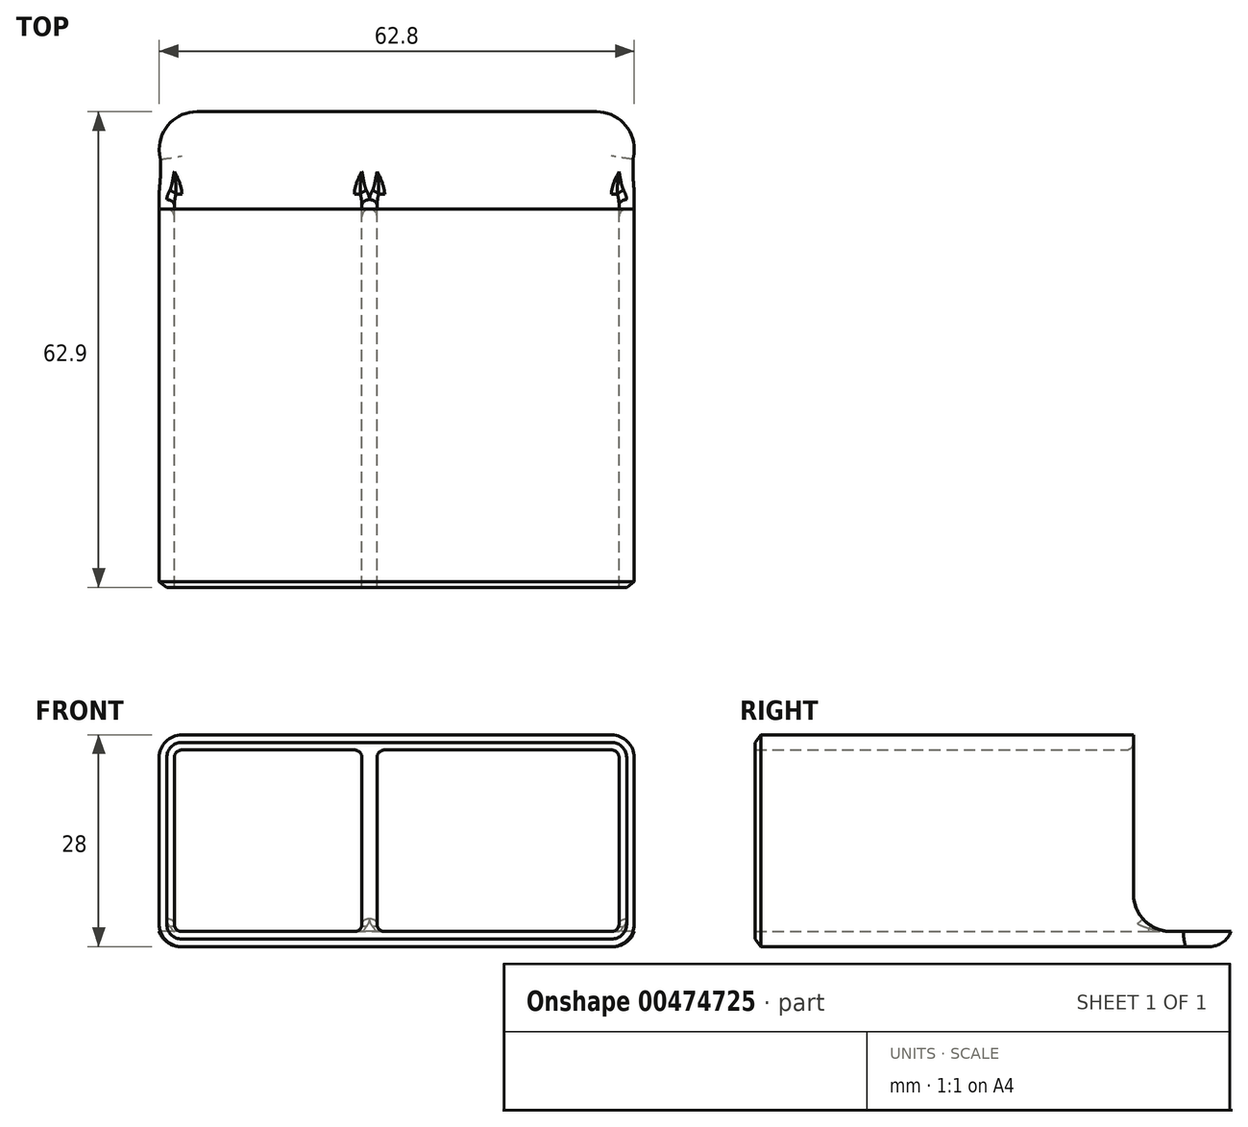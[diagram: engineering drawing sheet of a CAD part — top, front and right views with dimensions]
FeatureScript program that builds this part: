
annotation { "Feature Type Name" : "Feature", "Feature Type Description" : "" }
export const myFeature = defineFeature(function(context is Context, id is Id, definition is map)
    precondition{}
    {
        {
            var Q0;
            Q0=qCreatedBy(makeId("Front.planeOp"),FACE);
            var sketch = newSketch(context, id + "F0", { "sketchPlane" : qUnion([Q0])});
            skLineSegment(sketch, "E0.bottom", {"start": v(0, 0) * mm, "end": v(62.8, 0) * mm});
            skLineSegment(sketch, "E0.top", {"start": v(0, 28) * mm, "end": v(62.8, 28) * mm});
            skLineSegment(sketch, "E0.left", {"start": v(0, 0) * mm, "end": v(0, 28) * mm});
            skLineSegment(sketch, "E0.right", {"start": v(62.8, 0) * mm, "end": v(62.8, 28) * mm});
            skLineSegment(sketch, "E1.bottom", {"start": v(28.8, 26) * mm, "end": v(60.8, 26) * mm});
            skLineSegment(sketch, "E1.top", {"start": v(28.8, 2) * mm, "end": v(60.8, 2) * mm});
            skLineSegment(sketch, "E1.left", {"start": v(28.8, 26) * mm, "end": v(28.8, 2) * mm});
            skLineSegment(sketch, "E1.right", {"start": v(60.8, 26) * mm, "end": v(60.8, 2) * mm});
            skLineSegment(sketch, "E2.bottom", {"start": v(2, 26) * mm, "end": v(26.8, 26) * mm});
            skLineSegment(sketch, "E2.top", {"start": v(2, 2) * mm, "end": v(26.8, 2) * mm});
            skLineSegment(sketch, "E2.left", {"start": v(2, 26) * mm, "end": v(2, 2) * mm});
            skLineSegment(sketch, "E2.right", {"start": v(26.8, 26) * mm, "end": v(26.8, 2) * mm});
            skSolve(sketch);
        }
        {
            var Q0;
            Q0 = qSketchRegion(id + "F0", true);
            extrude(context, id + "F1", {"entities" : qUnion([Q0]), "depth" : 62.9 * mm, "offsetDistance" : 25 * mm});
        }
        {
            var Q0;
            Q0=makeQuery(id+"F1.opExtrude","SWEPT_FACE",FACE,{"disambiguationData":[OSD([sQuery(id+"F0.wireOp",EDGE,"E0.top")])]});
            var sketch = newSketch(context, id + "F2", { "sketchPlane" : qUnion([Q0])});
            skLineSegment(sketch, "E3.bottom", {"start": v(0, 0) * mm, "end": v(62.8, 0) * mm});
            skLineSegment(sketch, "E3.top", {"start": v(0, -12.9) * mm, "end": v(62.8, -12.9) * mm});
            skLineSegment(sketch, "E3.left", {"start": v(0, 0) * mm, "end": v(0, -12.9) * mm});
            skLineSegment(sketch, "E3.right", {"start": v(62.8, 0) * mm, "end": v(62.8, -12.9) * mm});
            skSolve(sketch);
        }
        {
            var Q0;
            Q0 = qSketchRegion(id + "F2", true);
            var Q1;
            Q1=makeQuery(id+"F1.opExtrude","SWEPT_FACE",FACE,{"disambiguationData":[OSD([sQuery(id+"F0.wireOp",EDGE,"E1.top")])]});
            extrude(context, id + "F3", {"entities" : qUnion([Q0]), "operationType" : NewBodyOperationType.REMOVE, "endBound" : BoundingType.UP_TO_SURFACE, "oppositeDirection" : true, "depth" : 25 * mm, "endBoundEntityFace" : qUnion([Q1]), "offsetDistance" : 25 * mm});
        }
        {
            var Q0;
            Q0=makeQuery(id+"F1.opExtrude","CAP_EDGE",EDGE,{"disambiguationData":[OSD([sQuery(id+"F0.wireOp",EDGE,"E0.right")])],"isStart":true});
            var Q1;
            Q1=makeQuery(id+"F1.opExtrude","CAP_EDGE",EDGE,{"disambiguationData":[OSD([sQuery(id+"F0.wireOp",EDGE,"E0.left")])],"isStart":true});
            fillet(context, id + "F4", {"entities" : qUnion([Q0, Q1]), "radius" : 5 * mm, "tangentPropagation" : true, "allowEdgeOverflow" : false});
        }
        {
            var Q0;
            {var subQ0=sQuery(id+"F2.wireOp",EDGE,"E3.top");Q0=makeQuery(id+"F3.boolean.opBoolean","COPY",EDGE,{"disambiguationData":[TD([makeQuery(id+"F1.opExtrude","SWEPT_FACE",FACE,{"disambiguationData":[OSD([sQuery(id+"F0.wireOp",EDGE,"E0.right")])]})])],"derivedFrom":makeQuery(id+"F3.opExtrude","CAP_EDGE",EDGE,{"disambiguationData":[OSD([subQ0])],"isStart":false})});}
            var Q1;
            {var subQ0=sQuery(id+"F2.wireOp",EDGE,"E3.top");Q1=makeQuery(id+"F3.boolean.opBoolean","COPY",EDGE,{"disambiguationData":[TD([makeQuery(id+"F1.opExtrude","SWEPT_FACE",FACE,{"disambiguationData":[OSD([sQuery(id+"F0.wireOp",EDGE,"E1.left")])]})])],"derivedFrom":makeQuery(id+"F3.opExtrude","CAP_EDGE",EDGE,{"disambiguationData":[OSD([subQ0])],"isStart":false})});}
            var Q2;
            {var subQ0=sQuery(id+"F2.wireOp",EDGE,"E3.top");Q2=makeQuery(id+"F3.boolean.opBoolean","COPY",EDGE,{"disambiguationData":[TD([makeQuery(id+"F1.opExtrude","SWEPT_FACE",FACE,{"disambiguationData":[OSD([sQuery(id+"F0.wireOp",EDGE,"E0.left")])]})])],"derivedFrom":makeQuery(id+"F3.opExtrude","CAP_EDGE",EDGE,{"disambiguationData":[OSD([subQ0])],"isStart":false})});}
            fillet(context, id + "F5", {"entities" : qUnion([Q0, Q1, Q2]), "radius" : 5 * mm, "tangentPropagation" : true, "allowEdgeOverflow" : false});
        }
        {
            var Q0;
            Q0=makeQuery(id+"F1.opExtrude","SWEPT_EDGE",EDGE,{"disambiguationData":[OSD([sQuery(id+"F0.wireOp",EDGE,"E1.top"),sQuery(id+"F0.wireOp",EDGE,"E1.right")])]});
            var Q1;
            Q1=makeQuery(id+"F1.opExtrude","SWEPT_EDGE",EDGE,{"disambiguationData":[OSD([sQuery(id+"F0.wireOp",EDGE,"E1.bottom"),sQuery(id+"F0.wireOp",EDGE,"E1.right")])]});
            var Q2;
            Q2=makeQuery(id+"F1.opExtrude","SWEPT_EDGE",EDGE,{"disambiguationData":[OSD([sQuery(id+"F0.wireOp",EDGE,"E1.bottom"),sQuery(id+"F0.wireOp",EDGE,"E1.left")])]});
            var Q3;
            Q3=makeQuery(id+"F1.opExtrude","SWEPT_EDGE",EDGE,{"disambiguationData":[OSD([sQuery(id+"F0.wireOp",EDGE,"E1.top"),sQuery(id+"F0.wireOp",EDGE,"E1.left")])]});
            var Q4;
            Q4=makeQuery(id+"F1.opExtrude","SWEPT_EDGE",EDGE,{"disambiguationData":[OSD([sQuery(id+"F0.wireOp",EDGE,"E2.top"),sQuery(id+"F0.wireOp",EDGE,"E2.right")])]});
            var Q5;
            Q5=makeQuery(id+"F1.opExtrude","SWEPT_EDGE",EDGE,{"disambiguationData":[OSD([sQuery(id+"F0.wireOp",EDGE,"E2.bottom"),sQuery(id+"F0.wireOp",EDGE,"E2.right")])]});
            var Q6;
            Q6=makeQuery(id+"F1.opExtrude","SWEPT_EDGE",EDGE,{"disambiguationData":[OSD([sQuery(id+"F0.wireOp",EDGE,"E2.bottom"),sQuery(id+"F0.wireOp",EDGE,"E2.left")])]});
            var Q7;
            Q7=makeQuery(id+"F1.opExtrude","SWEPT_EDGE",EDGE,{"disambiguationData":[OSD([sQuery(id+"F0.wireOp",EDGE,"E2.top"),sQuery(id+"F0.wireOp",EDGE,"E2.left")])]});
            fillet(context, id + "F6", {"entities" : qUnion([Q0, Q1, Q2, Q3, Q4, Q5, Q6, Q7]), "radius" : 1 * mm, "tangentPropagation" : true, "allowEdgeOverflow" : false});
        }
        {
            var Q0;
            Q0=makeQuery(id+"F1.opExtrude","SWEPT_EDGE",EDGE,{"disambiguationData":[OSD([sQuery(id+"F0.wireOp",EDGE,"E0.top"),sQuery(id+"F0.wireOp",EDGE,"E0.right")])]});
            var Q1;
            Q1=makeQuery(id+"F1.opExtrude","SWEPT_EDGE",EDGE,{"disambiguationData":[OSD([sQuery(id+"F0.wireOp",EDGE,"E0.top"),sQuery(id+"F0.wireOp",EDGE,"E0.left")])]});
            var Q2;
            Q2=makeQuery(id+"F1.opExtrude","CAP_EDGE",EDGE,{"disambiguationData":[OSD([sQuery(id+"F0.wireOp",EDGE,"E0.bottom")])],"isStart":true});
            fillet(context, id + "F7", {"entities" : qUnion([Q0, Q1, Q2]), "radius" : 3 * mm, "tangentPropagation" : true, "allowEdgeOverflow" : false});
        }
        {
            var Q0;
            Q0=makeQuery(id+"F3.boolean.opBoolean","INTERSECT",EDGE,{"derivedFrom":[makeQuery(id+"F1.opExtrude","SWEPT_FACE",FACE,{"disambiguationData":[OSD([sQuery(id+"F0.wireOp",EDGE,"E2.left")])]}),makeQuery(id+"F3.opExtrude","SWEPT_FACE",FACE,{"disambiguationData":[OSD([sQuery(id+"F2.wireOp",EDGE,"E3.top")])]})]});
            var Q1;
            Q1=makeQuery(id+"F3.boolean.opBoolean","INTERSECT",EDGE,{"derivedFrom":[makeQuery(id+"F1.opExtrude","SWEPT_FACE",FACE,{"disambiguationData":[OSD([sQuery(id+"F0.wireOp",EDGE,"E1.left")])]}),makeQuery(id+"F3.opExtrude","SWEPT_FACE",FACE,{"disambiguationData":[OSD([sQuery(id+"F2.wireOp",EDGE,"E3.top")])]})]});
            fillet(context, id + "F8", {"entities" : qUnion([Q0, Q1]), "radius" : 1 * mm, "tangentPropagation" : true, "allowEdgeOverflow" : false});
        }
        {
            var Q0;
            Q0=makeQuery(id+"F1.opExtrude","CAP_EDGE",EDGE,{"disambiguationData":[OSD([sQuery(id+"F0.wireOp",EDGE,"E0.left")])],"isStart":false});
            chamfer(context, id + "F9", {"entities" : qUnion([Q0]), "chamferType" : ChamferType.TWO_OFFSETS, "width1" : 1 * mm, "oppositeDirection" : false, "width2" : 0.75 * mm, "tangentPropagation" : true});
        }
    });
